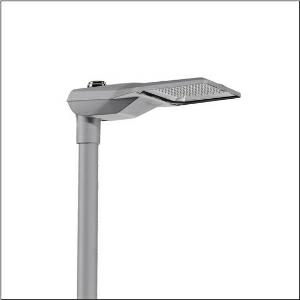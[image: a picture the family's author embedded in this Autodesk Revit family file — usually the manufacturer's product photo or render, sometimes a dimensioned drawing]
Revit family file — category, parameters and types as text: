
# Revit family: streetlight_sl_21_midi___st1_0a_5xe7d67n08mb_a1db
name_source: partatom
category: Lighting Fixtures
units: mm (PartAtom-declared; Revit-internal decimal feet)

## family parameters
Cut with Voids When Loaded = No
Host = Face
Light Source = No
Part Type = Normal
Room Calculation Point = No
Round Connector Dimension = Use Diameter
Shared = No

## types (1)
- --- (1 x LED, 16240 lm, 134.3 W, 2700K)
    Apparent Load = 134 VA
    CIE Flux Codes = 37 72 97 100 100
    Color Rendering = 70
    Color Temperature = 2700K
    Default Elevation = 1800 mm
    Description = Streetlight SL 21 midi, mast luminaire, primary light control with lens, of PMMA, primary optical cover: cover, of toughened safety glass, transparent, light distribution: ST1.0a, light emission: direct distribution, primary light characteristic: asymmetric, installation type: side-entry, LED, 3G 2.5mm², High Power LED, rated luminous flux: 16.240lm, luminous efficacy: 121lm/W, light colour: 727, colour temperature: 2700K, control gear: NEMA (7pin), control: overheat protection, pre-setting: linear dimming characteristic, constant luminous flux control, time-dependent luminous flux control, flexible luminous flux parameterisation, mains connection: 220..240V, AC, 50/60Hz, connection cable pre-assembled, cable length: 12,5m, wiring characteristics: H05VV-F, start of lifetime: 134W, end of service life: 141W, reduction: 60W, luminaire housing, of diecast aluminium (EN AC-44300), powder-coated, Siteco® metallic grey (DB 702S), corrosivity category C5 mid according to DIN EN ISO 12944, multi-level sealing system, sealing non-destructively replaceable, inclination adjustable: 0°, 5°, 10°, 15°, length: 644mm, width: 335mm, height: 110mm, spigot size: 42mm (side-entry), mounting height: 4..8m, protection rating (complete): IP66, insulation class (complete): insulation class I (protective earthing), certification: CE, ENEC, ENEC+, VDE, impact resistance: IK10, permissible operating ambient temperature for outdoor applications: -40..+50°C, standard-compliant lighting for roads and squares, packaging unit: 1 piece

Light Distribution: ST1.0a
    Height = 111 mm
    Lamp = 1 x LED
    Lamp Light Flux = 16240 lm
    Lamp Power = 134.3 W
    Lamp count = 1
    Length = 644 mm
    Luminous efficacy = 121 lm/W
    Manufacturer = Siteco
    ModVariant = No
    Model = 5XE7D67N08MB
    Number of Poles = 1
    OnlyDefault = Yes
    Power Factor = 1
    Product Name = Streetlight SL 21 midi | ST1.0a
    Product group = mast luminaire | pylon top
    ProductGroupID = 6100
    Protection Class = Protection class I
    Protection Degree = IP 66
    RLX_Detail_Level = 1
    RLX_Emergency_Light_Flux = 0 lm
    RLX_Emergency_Type = 0
    RLX_Emergency_Type_DB = No
    RlxData = <blob elided: 26453 chars, md5=fe709462>
    Socket = socket
    Standby Power = 0 W
    System Light Flux = 16240 lm
    System Power = 134 W
    Type Comments = factory setting: luminous flux: 100 % | dim-lin: 254 | 687 mA
    Type Image = l_1294377.jpg
    URL = http://relux.com
    VarID = @adj_157373
    Voltage = 0 V
    Weight = 0.00 kg
    Width = 336 mm

## geometry (parser evidence)
native form markers: Blend x4, Sweep x11
no freeform markers — native parametric forms only
